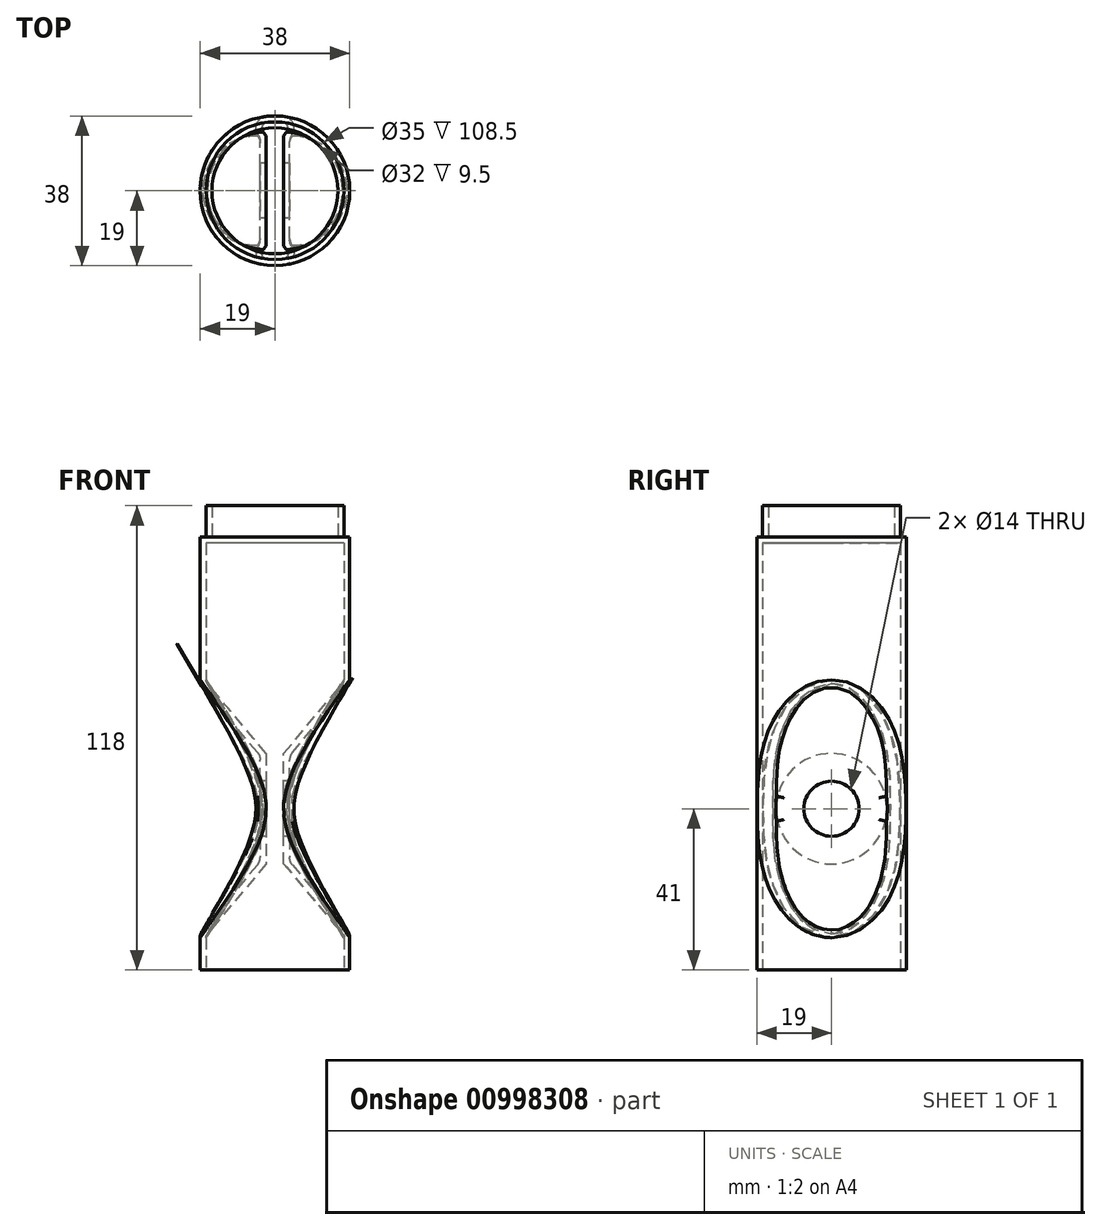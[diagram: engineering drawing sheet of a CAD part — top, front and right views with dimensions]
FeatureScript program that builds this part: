
annotation { "Feature Type Name" : "Feature", "Feature Type Description" : "" }
export const myFeature = defineFeature(function(context is Context, id is Id, definition is map)
    precondition{}
    {
        {
            var Q0;
            Q0=qCreatedBy(makeId("Top.planeOp"),FACE);
            var sketch = newSketch(context, id + "F0", { "sketchPlane" : qUnion([Q0])});
            skCircle(sketch, "E0", {"center": v(0, 0) * mm, "radius": 19 * mm});
            skSolve(sketch);
        }
        {
            var Q0;
            Q0=makeQuery(id+"F0.imprint","IMPRINT",FACE,{"disambiguationData":[TD([[makeQuery(id+"F0.imprint","IMPRINT",EDGE,{"derivedFrom":sQuery(id+"F0.wireOp",EDGE,"E0")}),1.0]])]});
            extrude(context, id + "F1", {"entities" : qUnion([Q0]), "depth" : 110 * mm, "offsetDistance" : 25 * mm});
        }
        {
            var Q0;
            Q0=makeQuery(id+"F1.opExtrude","CAP_FACE",FACE,{"disambiguationData":[OSD([sQuery(id+"F0.wireOp",EDGE,"E0")])],"isStart":false});
            var sketch = newSketch(context, id + "F2", { "sketchPlane" : qUnion([Q0])});
            skCircle(sketch, "E1", {"center": v(0, 0) * mm, "radius": 17.5 * mm});
            skSolve(sketch);
        }
        {
            var Q0;
            Q0 = qSketchRegion(id + "F2", true);
            extrude(context, id + "F3", {"entities" : qUnion([Q0]), "operationType" : NewBodyOperationType.ADD, "depth" : 8 * mm, "offsetDistance" : 25 * mm});
        }
        {
            var Q0;
            Q0=qCreatedBy(makeId("Front.planeOp"),FACE);
            var sketch = newSketch(context, id + "F4", { "sketchPlane" : qUnion([Q0])});
            skLineSegment(sketch, "E2", {"start": v(-33.93, 41) * mm, "end": v(-3.75, 41) * mm, "construction": true});
            skLineSegment(sketch, "E3", {"start": v(-27.31, 82.58) * mm, "end": v(-3.75, 54.5) * mm});
            skLineSegment(sketch, "E4", {"start": v(-3.75, 54.5) * mm, "end": v(-3.75, 41) * mm});
            skLineSegment(sketch, "E5", {"start": v(3.75, 41) * mm, "end": v(3.75, 54.5) * mm});
            skLineSegment(sketch, "E6", {"start": v(3.75, 54.5) * mm, "end": v(27.31, 82.58) * mm});
            skLineSegment(sketch, "E7", {"start": v(-27.31, 82.58) * mm, "end": v(-27.31, 41) * mm});
            skLineSegment(sketch, "E8", {"start": v(-27.31, 41) * mm, "end": v(-3.75, 41) * mm});
            skLineSegment(sketch, "E9", {"start": v(27.31, 41) * mm, "end": v(27.31, 82.58) * mm});
            skLineSegment(sketch, "E10", {"start": v(0, 0) * mm, "end": v(0, 130.55) * mm, "construction": true});
            skLineSegment(sketch, "E11.trimOffspring", {"start": v(3.75, 41) * mm, "end": v(38.25, 41) * mm, "construction": true});
            skLineSegment(sketch, "E12.trimOffspring", {"start": v(3.75, 41) * mm, "end": v(27.31, 41) * mm});
            skSolve(sketch);
        }
        {
            var Q0;
            Q0 = qSketchRegion(id + "F4", true);
            var Q1;
            Q1=sQuery(id+"F4.wireOp",EDGE,"E2");
            revolve(context, id + "F5", {"operationType" : NewBodyOperationType.REMOVE, "surfaceOperationType" : NewSurfaceOperationType.NEW, "entities" : qUnion([Q0]), "axis" : qUnion([Q1]), "revolveType" : RevolveType.FULL, "oppositeDirection" : true});
        }
        {
            var Q0;
            Q0=makeQuery(id+"F5.boolean.opBoolean","INTERSECT",EDGE,{"derivedFrom":[makeQuery(id+"F1.opExtrude","SWEPT_FACE",FACE,{"disambiguationData":[OSD([sQuery(id+"F0.wireOp",EDGE,"E0")])]}),makeQuery(id+"F5.opRevolve","SWEPT_FACE",FACE,{"disambiguationData":[OSD([sQuery(id+"F4.wireOp",EDGE,"E6")])]})]});
            var Q1;
            Q1=makeQuery(id+"F5.boolean.opBoolean","INTERSECT",EDGE,{"derivedFrom":[makeQuery(id+"F1.opExtrude","SWEPT_FACE",FACE,{"disambiguationData":[OSD([sQuery(id+"F0.wireOp",EDGE,"E0")])]}),makeQuery(id+"F5.opRevolve","SWEPT_FACE",FACE,{"disambiguationData":[OSD([sQuery(id+"F4.wireOp",EDGE,"E3")])]})]});
            fillet(context, id + "F6", {"entities" : qUnion([Q0, Q1]), "radius" : 3 * mm, "tangentPropagation" : true, "allowEdgeOverflow" : false});
        }
        {
            var Q0;
            Q0=makeQuery(id+"F3.opExtrude","CAP_FACE",FACE,{"disambiguationData":[OSD([sQuery(id+"F2.wireOp",EDGE,"E1")])],"isStart":false});
            var Q1;
            Q1=makeQuery(id+"F1.opExtrude","CAP_FACE",FACE,{"disambiguationData":[OSD([sQuery(id+"F0.wireOp",EDGE,"E0")])],"isStart":true});
            shell(context, id + "F7", {"entities" : qUnion([Q0, Q1]), "thickness" : 1.5 * mm});
        }
        {
            var Q0;
            Q0=makeQuery(id+"F5.boolean.opBoolean","COPY",EDGE,{"derivedFrom":makeQuery(id+"F5.opRevolve","SWEPT_EDGE",EDGE,{"disambiguationData":[OSD([sQuery(id+"F4.wireOp",EDGE,"E5"),sQuery(id+"F4.wireOp",EDGE,"E6")])]})});
            var Q1;
            Q1=makeQuery(id+"F5.boolean.opBoolean","COPY",EDGE,{"derivedFrom":makeQuery(id+"F5.opRevolve","SWEPT_EDGE",EDGE,{"disambiguationData":[OSD([sQuery(id+"F4.wireOp",EDGE,"E5"),sQuery(id+"F4.wireOp",EDGE,"E6")])]})});
            var Q2;
            Q2=makeQuery(id+"F6.opFillet","BLEND_EDGE",EDGE,{"disambiguationData":[OD(0.0)],"blendedFrom":[makeQuery(id+"F5.boolean.opBoolean","INTERSECT",EDGE,{"derivedFrom":[makeQuery(id+"F1.opExtrude","SWEPT_FACE",FACE,{"disambiguationData":[OSD([sQuery(id+"F0.wireOp",EDGE,"E0")])]}),makeQuery(id+"F5.opRevolve","SWEPT_FACE",FACE,{"disambiguationData":[OSD([sQuery(id+"F4.wireOp",EDGE,"E6")])]})]}),makeQuery(id+"F5.boolean.opBoolean","COPY",FACE,{"derivedFrom":makeQuery(id+"F5.opRevolve","SWEPT_FACE",FACE,{"disambiguationData":[OSD([sQuery(id+"F4.wireOp",EDGE,"E5")])]})})],"blendedInto":[makeQuery(id+"F5.boolean.opBoolean","COPY",FACE,{"derivedFrom":makeQuery(id+"F5.opRevolve","SWEPT_FACE",FACE,{"disambiguationData":[OSD([sQuery(id+"F4.wireOp",EDGE,"E5")])]})})]});
            var Q3;
            Q3=makeQuery(id+"F6.opFillet","BLEND_EDGE",EDGE,{"disambiguationData":[OD(1.0)],"blendedFrom":[makeQuery(id+"F5.boolean.opBoolean","INTERSECT",EDGE,{"derivedFrom":[makeQuery(id+"F1.opExtrude","SWEPT_FACE",FACE,{"disambiguationData":[OSD([sQuery(id+"F0.wireOp",EDGE,"E0")])]}),makeQuery(id+"F5.opRevolve","SWEPT_FACE",FACE,{"disambiguationData":[OSD([sQuery(id+"F4.wireOp",EDGE,"E6")])]})]}),makeQuery(id+"F5.boolean.opBoolean","COPY",FACE,{"derivedFrom":makeQuery(id+"F5.opRevolve","SWEPT_FACE",FACE,{"disambiguationData":[OSD([sQuery(id+"F4.wireOp",EDGE,"E5")])]})})],"blendedInto":[makeQuery(id+"F5.boolean.opBoolean","COPY",FACE,{"derivedFrom":makeQuery(id+"F5.opRevolve","SWEPT_FACE",FACE,{"disambiguationData":[OSD([sQuery(id+"F4.wireOp",EDGE,"E5")])]})})]});
            var Q4;
            Q4=makeQuery(id+"F5.boolean.opBoolean","COPY",EDGE,{"derivedFrom":makeQuery(id+"F5.opRevolve","SWEPT_EDGE",EDGE,{"disambiguationData":[OSD([sQuery(id+"F4.wireOp",EDGE,"E3"),sQuery(id+"F4.wireOp",EDGE,"E4")])]})});
            var Q5;
            Q5=makeQuery(id+"F6.opFillet","BLEND_EDGE",EDGE,{"disambiguationData":[OD(1.0)],"blendedFrom":[makeQuery(id+"F5.boolean.opBoolean","INTERSECT",EDGE,{"derivedFrom":[makeQuery(id+"F1.opExtrude","SWEPT_FACE",FACE,{"disambiguationData":[OSD([sQuery(id+"F0.wireOp",EDGE,"E0")])]}),makeQuery(id+"F5.opRevolve","SWEPT_FACE",FACE,{"disambiguationData":[OSD([sQuery(id+"F4.wireOp",EDGE,"E3")])]})]}),makeQuery(id+"F5.boolean.opBoolean","COPY",FACE,{"derivedFrom":makeQuery(id+"F5.opRevolve","SWEPT_FACE",FACE,{"disambiguationData":[OSD([sQuery(id+"F4.wireOp",EDGE,"E4")])]})})],"blendedInto":[makeQuery(id+"F5.boolean.opBoolean","COPY",FACE,{"derivedFrom":makeQuery(id+"F5.opRevolve","SWEPT_FACE",FACE,{"disambiguationData":[OSD([sQuery(id+"F4.wireOp",EDGE,"E4")])]})})]});
            var Q6;
            Q6=makeQuery(id+"F6.opFillet","BLEND_EDGE",EDGE,{"disambiguationData":[OD(0.0)],"blendedFrom":[makeQuery(id+"F5.boolean.opBoolean","INTERSECT",EDGE,{"derivedFrom":[makeQuery(id+"F1.opExtrude","SWEPT_FACE",FACE,{"disambiguationData":[OSD([sQuery(id+"F0.wireOp",EDGE,"E0")])]}),makeQuery(id+"F5.opRevolve","SWEPT_FACE",FACE,{"disambiguationData":[OSD([sQuery(id+"F4.wireOp",EDGE,"E3")])]})]}),makeQuery(id+"F5.boolean.opBoolean","COPY",FACE,{"derivedFrom":makeQuery(id+"F5.opRevolve","SWEPT_FACE",FACE,{"disambiguationData":[OSD([sQuery(id+"F4.wireOp",EDGE,"E4")])]})})],"blendedInto":[makeQuery(id+"F5.boolean.opBoolean","COPY",FACE,{"derivedFrom":makeQuery(id+"F5.opRevolve","SWEPT_FACE",FACE,{"disambiguationData":[OSD([sQuery(id+"F4.wireOp",EDGE,"E4")])]})})]});
            fillet(context, id + "F8", {"entities" : qUnion([Q0, Q1, Q2, Q3, Q4, Q5, Q6]), "radius" : 3 * mm, "tangentPropagation" : true, "allowEdgeOverflow" : false});
        }
        {
            var Q0;
            Q0=makeQuery(id+"F5.boolean.opBoolean","COPY",FACE,{"derivedFrom":makeQuery(id+"F5.opRevolve","SWEPT_FACE",FACE,{"disambiguationData":[OSD([sQuery(id+"F4.wireOp",EDGE,"E4")])]})});
            var sketch = newSketch(context, id + "F9", { "sketchPlane" : qUnion([Q0])});
            skCircle(sketch, "E13", {"center": v(0, 41) * mm, "radius": 7 * mm});
            skSolve(sketch);
        }
        {
            var Q0;
            Q0 = qSketchRegion(id + "F9", true);
            extrude(context, id + "F10", {"entities" : qUnion([Q0]), "operationType" : NewBodyOperationType.REMOVE, "oppositeDirection" : true, "depth" : 25 * mm, "offsetDistance" : 25 * mm});
        }
    });
